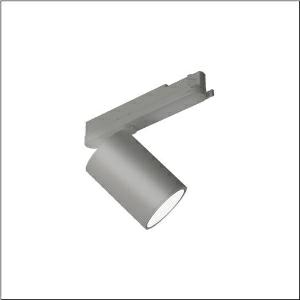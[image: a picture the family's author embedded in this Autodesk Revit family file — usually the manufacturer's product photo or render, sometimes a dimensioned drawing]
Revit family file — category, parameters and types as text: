
# Revit family: spot_31_51sf62mab4b
name_source: partatom
category: Lighting Fixtures
units: mm (PartAtom-declared; Revit-internal decimal feet)

## family parameters
Cut with Voids When Loaded = No
Host = Face
Light Source = No
Part Type = Normal
Room Calculation Point = No
Round Connector Dimension = Use Diameter
Shared = No

## types (1)
- --- (1 x LED, 4980 lm, 41.8 W, 3000K)
    Apparent Load = 42 VA
    CIE Flux Codes = 93 97 99 100 100
    Color Rendering = 90
    Color Temperature = 3000K
    Default Elevation = 1800 mm
    Description = Spot 31, directional spotlight, light control with lens, of PMMA, LED rated luminous flux: 4.790lm, light colour: 930, control gear: ECG Multilumen, with 3-phase adapter, mains connection: 220..240V, AC, 50/60Hz, of aluminium, metallic grey (RAL 9006), length: 213mm, diameter: 90mm, protection rating (complete): IP20, insulation class (complete): insulation class I (protective earthing), certification: CE, impact resistance: IK02, permissible ambient temperature for indoor applications: -20..+40°C, packaging unit: 1 piece
    Height = 175 mm
    Lamp = 1 x LED
    Lamp Light Flux = 4980 lm
    Lamp Power = 41.8 W
    Lamp count = 1
    Length = 90 mm
    Luminous efficacy = 119 lm/W
    Manufacturer = Siteco
    ModVariant = No
    Model = 51SF62MAB4B
    Mounting Place = Ceiling
    Mounting Type = Pendant
    Number of Poles = 1
    OnlyDefault = Yes
    Power Factor = 1
    Product Name = Spot 31
    Product group = directional spotlight
    ProductGroupID = 905
    Protection Class = Protection class I
    Protection Degree = IP 20
    RLX_Detail_Level = 1
    RLX_Emergency_Light_Flux = 0 lm
    RLX_Emergency_Type = 0
    RLX_Emergency_Type_DB = No
    RlxData = <blob elided: 20033 chars, md5=cfec5e8c>
    Socket = socket
    Standby Power = 0 W
    System Light Flux = 4980 lm
    System Power = 42 W
    Type Comments = factory setting: luminous flux: 100 % | (ON | ON | ON | ON) | 1050 mA
    Type Image = l_1273725.jpg
    URL = http://relux.com
    VarID = @adj_096179
    Voltage = 0 V
    Weight = 0.00 kg
    Width = 0 mm  [stored 0 ft]

note: [stored X ft] marks values corroborated as IEEE doubles in the binary element streams (Revit-internal decimal feet)

## geometry (parser evidence)
native form markers: Blend x4, Sweep x10
no freeform markers — native parametric forms only
